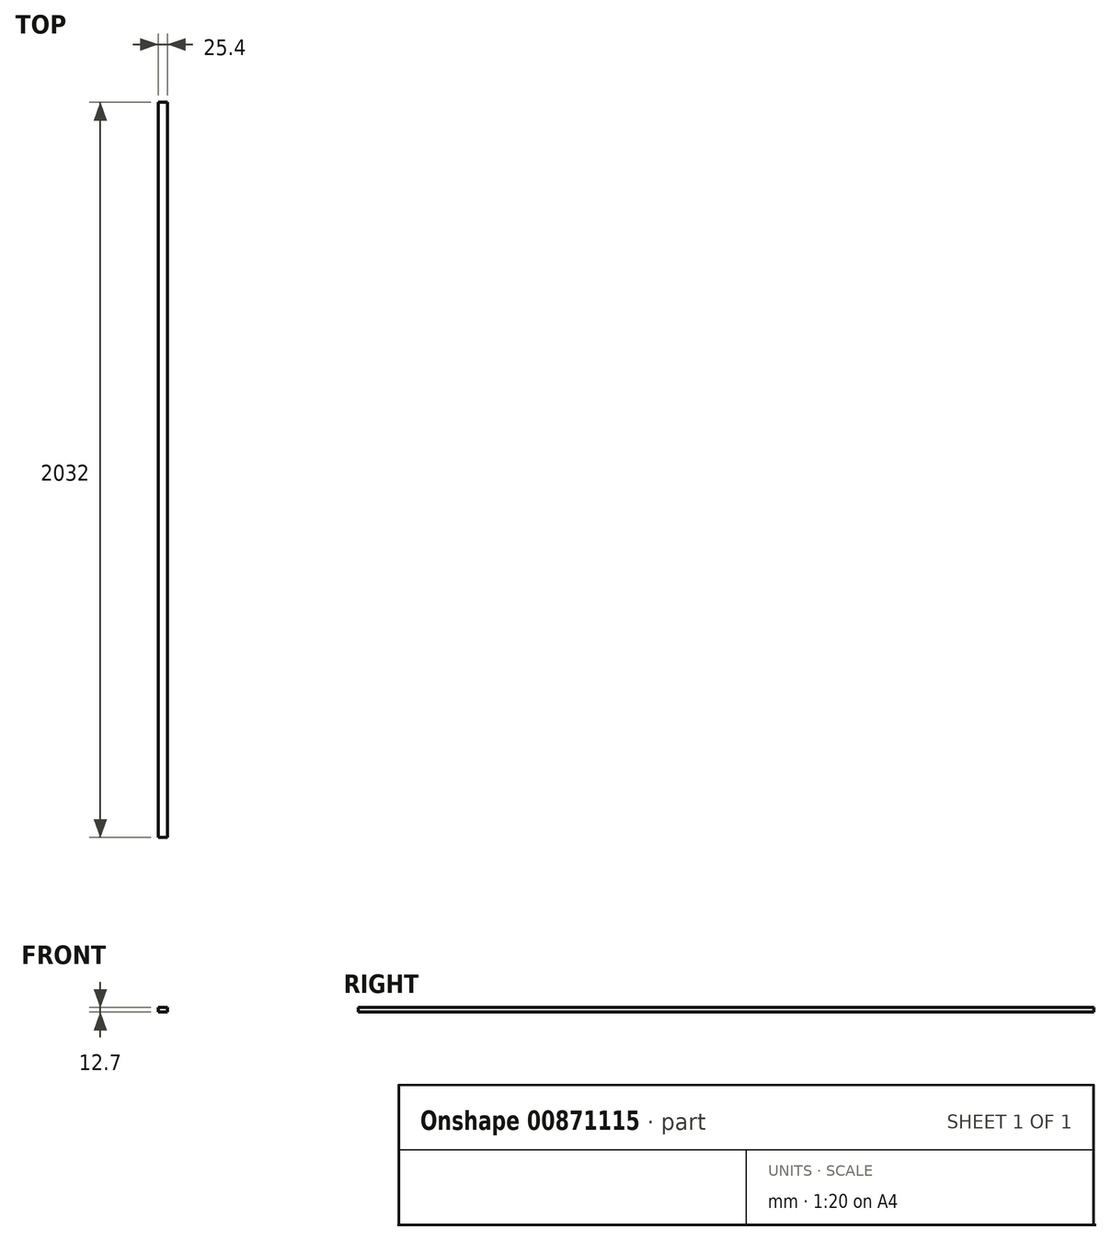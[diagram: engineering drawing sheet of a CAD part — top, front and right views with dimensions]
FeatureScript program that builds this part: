
annotation { "Feature Type Name" : "Feature", "Feature Type Description" : "" }
export const myFeature = defineFeature(function(context is Context, id is Id, definition is map)
    precondition{}
    {
        {
            var Q0;
            Q0=qCreatedBy(makeId("Front.planeOp"),FACE);
            var sketch = newSketch(context, id + "F0", { "sketchPlane" : qUnion([Q0])});
            skLineSegment(sketch, "E0.bottom", {"start": v(0, 0) * mm, "end": v(25.4, 0) * mm});
            skLineSegment(sketch, "E0.top", {"start": v(0, 12.7) * mm, "end": v(25.4, 12.7) * mm});
            skLineSegment(sketch, "E0.left", {"start": v(0, 0) * mm, "end": v(0, 12.7) * mm});
            skLineSegment(sketch, "E0.right", {"start": v(25.4, 0) * mm, "end": v(25.4, 12.7) * mm});
            skSolve(sketch);
        }
        {
            var Q0;
            Q0 = qSketchRegion(id + "F0", true);
            extrude(context, id + "F1", {"entities" : qUnion([Q0]), "depth" : 2032 * mm, "offsetDistance" : 25.4 * mm});
        }
    });
